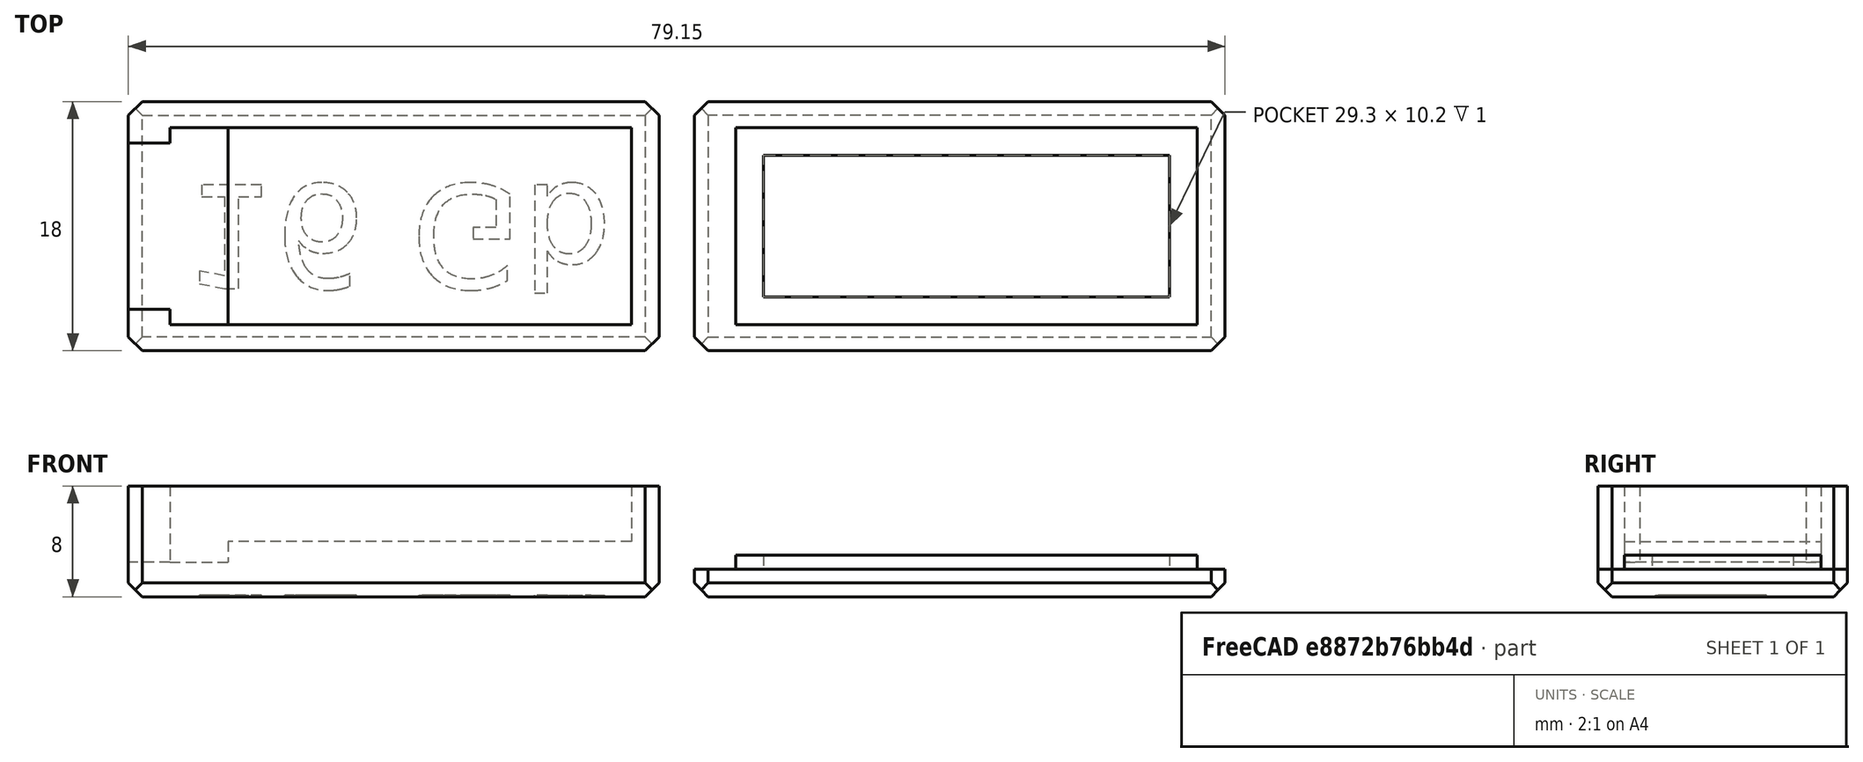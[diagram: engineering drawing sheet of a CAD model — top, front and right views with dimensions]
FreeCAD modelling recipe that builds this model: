
FCSTD DOCUMENT  (FreeCAD 0.21R33668 +26 (Git))
Label: flash_Case
License: All rights reserved
LicenseURL: http://en.wikipedia.org/wiki/All_rights_reserved
objects: TechDraw::DrawViewDimension×17, Sketcher::SketchObject×6, PartDesign::Pocket×4, PartDesign::Chamfer×4, PartDesign::Pad×3, PartDesign::Body×2, TechDraw::DrawViewPart×2, Part::Part2DObjectPython×1, TechDraw::DrawSVGTemplate×1, TechDraw::DrawPage×1
note: 59 computed .brp shape members not serialized (recipe doc carries the construction recipe); baked Part::Feature solids carry a one-line shape summary decoded from their .brp

FEATURE [Sketcher::SketchObject] Sketch
  FullyConstrained = true
  MapMode = 5
  Support = -> [XY_Plane]
  sketch-geometry (4):
    g0: LineSegment StartX=0 StartY=9 StartZ=0 EndX=38.3 EndY=9 EndZ=0
    g1: LineSegment StartX=38.3 StartY=9 StartZ=0 EndX=38.3 EndY=-9 EndZ=0
    g2: LineSegment StartX=38.3 StartY=-9 StartZ=0 EndX=0 EndY=-9 EndZ=0
    g3: LineSegment StartX=0 StartY=-9 StartZ=0 EndX=0 EndY=9 EndZ=0
  constraints (11):
    c: Coincident(g0,g1)
    c: Coincident(g1,g2)
    c: Coincident(g2,g3)
    c: Coincident(g3,g0)
    c: Horizontal(g0)
    c: Horizontal(g2)
    c: Vertical(g1)
    c: Vertical(g3)
    c: DistanceX(g0,g0) = 38.3
    c: DistanceY(g1,g1) = 18
    c: Symmetric(g0,g2,g-1)
FEATURE [PartDesign::Pad] Pad
  Direction = (0,0,1)
  Length = 8
  Length2 = 10
  Profile = -> Sketch
  ReferenceAxis = -> Sketch [N_Axis]
  Type = 0
FEATURE [Sketcher::SketchObject] Sketch001
  ExternalGeometry = -> [Pad]
  FullyConstrained = true
  MapMode = 5
  Placement = pos=(0,0,8) rot=(0,0,1;0rad)
  Support = -> [Pad]
  sketch-geometry (9):
    g0: LineSegment StartX=0 StartY=6 StartZ=0 EndX=0 EndY=-6 EndZ=0
    g1: LineSegment StartX=0 StartY=-6 StartZ=0 EndX=3 EndY=-6 EndZ=0
    g2: LineSegment StartX=3 StartY=6 StartZ=0 EndX=0 EndY=6 EndZ=0
    g3: GeomPoint X=1.5 Y=0 Z=0
    g4: LineSegment StartX=3 StartY=6 StartZ=0 EndX=3 EndY=7.1 EndZ=0
    g5: LineSegment StartX=3 StartY=7.1 StartZ=0 EndX=7.2 EndY=7.1 EndZ=0
    g6: LineSegment StartX=7.2 StartY=7.1 StartZ=0 EndX=7.2 EndY=-7.1 EndZ=0
    g7: LineSegment StartX=7.2 StartY=-7.1 StartZ=0 EndX=3 EndY=-7.1 EndZ=0
    g8: LineSegment StartX=3 StartY=-7.1 StartZ=0 EndX=3 EndY=-6 EndZ=0
  constraints (25):
    c: Coincident(g0,g1)
    c: Coincident(g2,g0)
    c: Horizontal(g1)
    c: Horizontal(g2)
    c: Vertical(g0)
    c: Symmetric(g1,g0,g3)
    c: PointOnObject(g3,g-1)
    c: PointOnObject(g0,g-3)
    c: DistanceY(g0,g0) = 12
    c: DistanceX(g2,g2) = 3
    c: Equal(g1,g2)
    c: Vertical(g4)
    c: Coincident(g4,g5)
    c: Horizontal(g5)
    c: Coincident(g5,g6)
    c: Vertical(g6)
    c: Coincident(g6,g7)
    c: Horizontal(g7)
    c: Coincident(g7,g8)
    c: Coincident(g4,g2)
    c: Coincident(g8,g1)
    c: DistanceY(g6,g5) = 14.2
    c: DistanceX(g4,g5) = 4.2
    c: Vertical(g8)
    c: Equal(g8,g4)
FEATURE [PartDesign::Pocket] Pocket
  BaseFeature = -> Pad
  Direction = (0,0,-1)
  Length = 5.5
  Length2 = 5
  Profile = -> Sketch001
  ReferenceAxis = -> Sketch001 [N_Axis]
  Type = 0
FEATURE [Sketcher::SketchObject] Sketch002
  ExternalGeometry = -> [Pocket]
  FullyConstrained = true
  MapMode = 5
  Placement = pos=(0,0,8) rot=(0,0,1;0rad)
  Support = -> [Pocket]
  sketch-geometry (5):
    g0: LineSegment StartX=36.3 StartY=-7.1 StartZ=0 EndX=36.3 EndY=7.1 EndZ=0
    g1: LineSegment StartX=36.3 StartY=7.1 StartZ=0 EndX=7.2 EndY=7.1 EndZ=0
    g2: LineSegment StartX=7.2 StartY=7.1 StartZ=0 EndX=7.2 EndY=-7.1 EndZ=0
    g3: LineSegment StartX=7.2 StartY=-7.1 StartZ=0 EndX=36.3 EndY=-7.1 EndZ=0
    g4: GeomPoint X=21.75 Y=0 Z=0
  constraints (12):
    c: Coincident(g0,g1)
    c: Coincident(g1,g2)
    c: Coincident(g2,g3)
    c: Coincident(g3,g0)
    c: Horizontal(g1)
    c: Horizontal(g3)
    c: Vertical(g0)
    c: Vertical(g2)
    c: Symmetric(g1,g0,g4)
    c: PointOnObject(g4,g-1)
    c: Coincident(g1,g-3)
    c: DistanceX(g1,g1) = 29.1
FEATURE [PartDesign::Pocket] Pocket001
  BaseFeature = -> Pocket
  Direction = (0,0,-1)
  Length = 4
  Length2 = 5
  Profile = -> Sketch002
  ReferenceAxis = -> Sketch002 [N_Axis]
  Type = 0
FEATURE [PartDesign::Chamfer] Chamfer
  Angle = 45
  Base = -> Pocket001 [Edge3,Edge5,Edge15,Edge13]
  BaseFeature = -> Pocket001
  ChamferType = 0
  FlipDirection = false
  Size = 1
  Size2 = 1
  SupportTransform = false
  UseAllEdges = false
FEATURE [PartDesign::Chamfer] Chamfer001
  Angle = 45
  Base = -> Chamfer [Edge7,Edge27,Edge4,Edge1]
  BaseFeature = -> Chamfer
  ChamferType = 0
  FlipDirection = false
  Size = 1
  Size2 = 1
  SupportTransform = false
  UseAllEdges = false
FEATURE [Sketcher::SketchObject] Sketch003
  FullyConstrained = true
  MapMode = 5
  Support = -> [XY_Plane001]
  sketch-geometry (5):
    g0: LineSegment StartX=79.15 StartY=-9 StartZ=0 EndX=79.15 EndY=9 EndZ=0
    g1: LineSegment StartX=79.15 StartY=9 StartZ=0 EndX=40.85 EndY=9 EndZ=0
    g2: LineSegment StartX=40.85 StartY=9 StartZ=0 EndX=40.85 EndY=-9 EndZ=0
    g3: LineSegment StartX=40.85 StartY=-9 StartZ=0 EndX=79.15 EndY=-9 EndZ=0
    g4: GeomPoint X=60 Y=0 Z=0
  constraints (13):
    c: Coincident(g0,g1)
    c: Coincident(g1,g2)
    c: Coincident(g2,g3)
    c: Coincident(g3,g0)
    c: Horizontal(g1)
    c: Horizontal(g3)
    c: Vertical(g0)
    c: Vertical(g2)
    c: Symmetric(g1,g0,g4)
    c: PointOnObject(g4,g-1)
    c: DistanceX(g1,g1) = 38.3
    c: DistanceY(g2,g2) = 18
    c: DistanceX(g-1,g4) = 60
FEATURE [PartDesign::Pad] Pad001
  Direction = (0,0,1)
  Length = 2
  Length2 = 10
  Profile = -> Sketch003
  ReferenceAxis = -> Sketch003 [N_Axis]
  Type = 0
FEATURE [PartDesign::Chamfer] Chamfer002
  Angle = 45
  Base = -> Pad001 [Edge6,Edge9,Edge11,Edge3]
  BaseFeature = -> Pad001
  ChamferType = 0
  FlipDirection = false
  Size = 1
  Size2 = 1
  SupportTransform = false
  UseAllEdges = false
FEATURE [PartDesign::Chamfer] Chamfer003
  Angle = 45
  Base = -> Chamfer002 [Edge4,Edge14,Edge1,Edge5]
  BaseFeature = -> Chamfer002
  ChamferType = 0
  FlipDirection = false
  Size = 1
  Size2 = 1
  SupportTransform = false
  UseAllEdges = false
FEATURE [Sketcher::SketchObject] Sketch004
  ExternalGeometry = -> [Chamfer003]
  FullyConstrained = true
  MapMode = 5
  Placement = pos=(0,0,2) rot=(0,0,1;0rad)
  Support = -> [Chamfer003]
  sketch-geometry (5):
    g0: LineSegment StartX=43.85 StartY=7.1 StartZ=0 EndX=43.85 EndY=-7.1 EndZ=0
    g1: LineSegment StartX=43.85 StartY=-7.1 StartZ=0 EndX=77.15 EndY=-7.1 EndZ=0
    g2: LineSegment StartX=77.15 StartY=-7.1 StartZ=0 EndX=77.15 EndY=7.1 EndZ=0
    g3: LineSegment StartX=77.15 StartY=7.1 StartZ=0 EndX=43.85 EndY=7.1 EndZ=0
    g4: GeomPoint X=60.5 Y=3e-16 Z=0
  constraints (13):
    c: Coincident(g0,g1)
    c: Coincident(g1,g2)
    c: Coincident(g2,g3)
    c: Coincident(g3,g0)
    c: Horizontal(g1)
    c: Horizontal(g3)
    c: Vertical(g0)
    c: Vertical(g2)
    c: Symmetric(g1,g0,g4)
    c: PointOnObject(g4,g-1)
    c: DistanceX(g-3,g0) = 3
    c: DistanceX(g3,g3) = 33.3
    c: DistanceY(g1,g2) = 14.2
FEATURE [PartDesign::Pad] Pad002
  BaseFeature = -> Chamfer003
  Direction = (0,0,1)
  Length = 1
  Length2 = 10
  Profile = -> Sketch004
  ReferenceAxis = -> Sketch004 [N_Axis]
  Type = 0
FEATURE [Sketcher::SketchObject] Sketch005
  ExternalGeometry = -> [Pad002]
  FullyConstrained = true
  MapMode = 5
  Placement = pos=(0,0,3) rot=(0,0,1;0rad)
  Support = -> [Pad002]
  sketch-geometry (5):
    g0: LineSegment StartX=75.15 StartY=-5.1 StartZ=0 EndX=75.15 EndY=5.1 EndZ=0
    g1: LineSegment StartX=75.15 StartY=5.1 StartZ=0 EndX=45.85 EndY=5.1 EndZ=0
    g2: LineSegment StartX=45.85 StartY=5.1 StartZ=0 EndX=45.85 EndY=-5.1 EndZ=0
    g3: LineSegment StartX=45.85 StartY=-5.1 StartZ=0 EndX=75.15 EndY=-5.1 EndZ=0
    g4: GeomPoint X=60.5 Y=0 Z=0
  constraints (13):
    c: Coincident(g0,g1)
    c: Coincident(g1,g2)
    c: Coincident(g2,g3)
    c: Coincident(g3,g0)
    c: Horizontal(g1)
    c: Horizontal(g3)
    c: Vertical(g0)
    c: Vertical(g2)
    c: Symmetric(g1,g0,g4)
    c: PointOnObject(g4,g-1)
    c: DistanceX(g-3,g1) = 2
    c: Distance(g0,g-4) = 2
    c: Distance(g0,g-5) = 2
FEATURE [PartDesign::Pocket] Pocket002
  BaseFeature = -> Pad002
  Direction = (0,0,-1)
  Length = 1
  Length2 = 5
  Profile = -> Sketch005
  ReferenceAxis = -> Sketch005 [N_Axis]
  Type = 0
FEATURE [PartDesign::Body] Body001  label="Cover"
  Group = -> [Sketch003,Pad001,Chamfer002,Chamfer003,Sketch004,Pad002,Sketch005,Pocket002]
  Origin = -> Origin001
  Tip = -> Pocket002
FEATURE [Part::Part2DObjectPython] ShapeString  # Draft 2D object (typed FeaturePython)
  FontFile = <path>
  MakeFace = true
  Placement = pos=(4,3,0) rot=(1,0,0;3.14159rad)
  Size = 8
  String = 16 Gb
  Tracking = 0
FEATURE [PartDesign::Pocket] Pocket003
  BaseFeature = -> Chamfer001
  Direction = (0,0,1)
  Length = 0.1
  Length2 = 5
  Profile = -> ShapeString
  ReferenceAxis = -> ShapeString [N_Axis]
  Type = 0
FEATURE [PartDesign::Body] Body  label="Тело"
  Group = -> [Sketch,Pad,Sketch001,Pocket,Sketch002,Pocket001,Chamfer,Chamfer001,ShapeString,Pocket003]
  Origin = -> Origin
  Tip = -> Pocket003
FEATURE [TechDraw::DrawSVGTemplate] Template
  Height = 210
  Orientation = 1
  Template = C:/Program Files/FreeCAD 0.21/data/Mod/TechDraw/Templates/A4_Landscape_blank.svg
  Width = 297
FEATURE [TechDraw::DrawViewPart] View001
  CoarseView = false
  Direction = (0,0,1)
  Focus = 100
  HardHidden = false
  IsoCount = 0
  IsoHidden = false
  IsoVisible = false
  LockPosition = false
  Perspective = false
  Rotation = 0
  Scale = 4
  ScaleType = 2
  ScrubCount = 0
  SeamHidden = false
  SeamVisible = false
  SmoothHidden = false
  SmoothVisible = true
  Source = -> [Pocket003]
  X = 133.304
  XDirection = (1,0,0)
  Y = 154.662
FEATURE [TechDraw::DrawViewDimension] Dimension
  AngleOverride = false
  Arbitrary = false
  ArbitraryTolerances = false
  EqualTolerance = true
  ExtensionAngle = 0
  FormatSpec = %.2w
  FormatSpecOverTolerance = %+.2w
  FormatSpecUnderTolerance = %+.2w
  Inverted = false
  LineAngle = 0
  LockPosition = false
  MeasureType = 1
  OverTolerance = 0
  References2D = -> [View001]
  Rotation = 0
  ScaleType = 0
  TheoreticalExact = false
  Type = 1
  UnderTolerance = 0
  X = 2.26455
  Y = -16.8084
FEATURE [TechDraw::DrawViewDimension] Dimension001
  AngleOverride = false
  Arbitrary = false
  ArbitraryTolerances = false
  EqualTolerance = true
  ExtensionAngle = 0
  FormatSpec = %.2w
  FormatSpecOverTolerance = %+.2w
  FormatSpecUnderTolerance = %+.2w
  Inverted = false
  LineAngle = 0
  LockPosition = false
  MeasureType = 1
  OverTolerance = 0
  References2D = -> [View001]
  Rotation = 0
  ScaleType = 0
  TheoreticalExact = false
  Type = 2
  UnderTolerance = 0
  X = 58.4585
  Y = 2.75519
FEATURE [TechDraw::DrawViewDimension] Dimension002
  AngleOverride = false
  Arbitrary = false
  ArbitraryTolerances = false
  EqualTolerance = true
  ExtensionAngle = 0
  FormatSpec = %.2w
  FormatSpecOverTolerance = %+.2w
  FormatSpecUnderTolerance = %+.2w
  Inverted = false
  LineAngle = 0
  LockPosition = false
  MeasureType = 1
  OverTolerance = 0
  References2D = -> [View001]
  Rotation = 0
  ScaleType = 0
  TheoreticalExact = false
  Type = 2
  UnderTolerance = 0
  X = -86.5106
  Y = 1.29138
FEATURE [TechDraw::DrawViewDimension] Dimension003
  AngleOverride = false
  Arbitrary = false
  ArbitraryTolerances = false
  EqualTolerance = true
  ExtensionAngle = 0
  FormatSpec = %.2w
  FormatSpecOverTolerance = %+.2w
  FormatSpecUnderTolerance = %+.2w
  Inverted = false
  LineAngle = 0
  LockPosition = false
  MeasureType = 1
  OverTolerance = 0
  References2D = -> [View001]
  Rotation = 0
  ScaleType = 0
  TheoreticalExact = false
  Type = 2
  UnderTolerance = 0
  X = 108.447
  Y = 6.35612
FEATURE [TechDraw::DrawViewDimension] Dimension004
  AngleOverride = false
  Arbitrary = false
  ArbitraryTolerances = false
  EqualTolerance = true
  ExtensionAngle = 0
  FormatSpec = %.2w
  FormatSpecOverTolerance = %+.2w
  FormatSpecUnderTolerance = %+.2w
  Inverted = false
  LineAngle = 0
  LockPosition = false
  MeasureType = 1
  OverTolerance = 0
  References2D = -> [View001]
  Rotation = 0
  ScaleType = 0
  TheoreticalExact = false
  Type = 1
  UnderTolerance = 0
  X = -71.1553
  Y = 24.4729
FEATURE [TechDraw::DrawViewDimension] Dimension005
  AngleOverride = false
  Arbitrary = false
  ArbitraryTolerances = false
  EqualTolerance = true
  ExtensionAngle = 0
  FormatSpec = %.2w
  FormatSpecOverTolerance = %+.2w
  FormatSpecUnderTolerance = %+.2w
  Inverted = false
  LineAngle = 0
  LockPosition = false
  MeasureType = 1
  OverTolerance = 0
  References2D = -> [View001]
  Rotation = 0
  ScaleType = 0
  TheoreticalExact = false
  Type = 1
  UnderTolerance = 0
  X = -56.2
  Y = 24.2526
FEATURE [TechDraw::DrawViewDimension] Dimension006
  AngleOverride = false
  Arbitrary = false
  ArbitraryTolerances = false
  EqualTolerance = true
  ExtensionAngle = 0
  FormatSpec = %.2w
  FormatSpecOverTolerance = %+.2w
  FormatSpecUnderTolerance = %+.2w
  Inverted = false
  LineAngle = 0
  LockPosition = false
  MeasureType = 1
  OverTolerance = 0
  References2D = -> [View001]
  Rotation = 0
  ScaleType = 0
  TheoreticalExact = false
  Type = 1
  UnderTolerance = 0
  X = 73.9929
  Y = -34.4885
FEATURE [TechDraw::DrawViewDimension] Dimension007
  AngleOverride = false
  Arbitrary = false
  ArbitraryTolerances = false
  EqualTolerance = true
  ExtensionAngle = 0
  FormatSpec = %.2w
  FormatSpecOverTolerance = %+.2w
  FormatSpecUnderTolerance = %+.2w
  Inverted = false
  LineAngle = 0
  LockPosition = false
  MeasureType = 1
  OverTolerance = 0
  References2D = -> [View001]
  Rotation = 0
  ScaleType = 0
  TheoreticalExact = false
  Type = 1
  UnderTolerance = 0
  X = -1.1914
  Y = 50.0302
FEATURE [TechDraw::DrawViewPart] View
  CoarseView = false
  Direction = (0,0,1)
  Focus = 100
  HardHidden = false
  IsoCount = 0
  IsoHidden = false
  IsoVisible = false
  LockPosition = false
  Perspective = false
  Rotation = 0
  Scale = 2
  ScaleType = 2
  ScrubCount = 0
  SeamHidden = false
  SeamVisible = false
  SmoothHidden = false
  SmoothVisible = true
  Source = -> [Body001]
  X = 120.621
  XDirection = (1,0,0)
  Y = 61.8661
FEATURE [TechDraw::DrawViewDimension] Dimension008
  AngleOverride = false
  Arbitrary = false
  ArbitraryTolerances = false
  EqualTolerance = true
  ExtensionAngle = 0
  FormatSpec = %.2w
  FormatSpecOverTolerance = %+.2w
  FormatSpecUnderTolerance = %+.2w
  Inverted = false
  LineAngle = 0
  LockPosition = false
  MeasureType = 1
  OverTolerance = 0
  References2D = -> [View]
  Rotation = 0
  ScaleType = 0
  TheoreticalExact = false
  Type = 2
  UnderTolerance = 0
  X = 68.3874
  Y = 3.55205
FEATURE [TechDraw::DrawViewDimension] Dimension009
  AngleOverride = false
  Arbitrary = false
  ArbitraryTolerances = false
  EqualTolerance = true
  ExtensionAngle = 0
  FormatSpec = %.2w
  FormatSpecOverTolerance = %+.2w
  FormatSpecUnderTolerance = %+.2w
  Inverted = false
  LineAngle = 0
  LockPosition = false
  MeasureType = 1
  OverTolerance = 0
  References2D = -> [View]
  Rotation = 0
  ScaleType = 0
  TheoreticalExact = false
  Type = 2
  UnderTolerance = 0
  X = 49.0286
  Y = 18.6
FEATURE [TechDraw::DrawViewDimension] Dimension010
  AngleOverride = false
  Arbitrary = false
  ArbitraryTolerances = false
  EqualTolerance = true
  ExtensionAngle = 0
  FormatSpec = %.2w
  FormatSpecOverTolerance = %+.2w
  FormatSpecUnderTolerance = %+.2w
  Inverted = false
  LineAngle = 0
  LockPosition = false
  MeasureType = 1
  OverTolerance = 0
  References2D = -> [View]
  Rotation = 0
  ScaleType = 0
  TheoreticalExact = false
  Type = 2
  UnderTolerance = 0
  X = 59.9833
  Y = 14.1619
FEATURE [TechDraw::DrawViewDimension] Dimension011
  AngleOverride = false
  Arbitrary = false
  ArbitraryTolerances = false
  EqualTolerance = true
  ExtensionAngle = 0
  FormatSpec = %.2w
  FormatSpecOverTolerance = %+.2w
  FormatSpecUnderTolerance = %+.2w
  Inverted = false
  LineAngle = 0
  LockPosition = false
  MeasureType = 1
  OverTolerance = 0
  References2D = -> [View]
  Rotation = 0
  ScaleType = 0
  TheoreticalExact = false
  Type = 1
  UnderTolerance = 0
  X = 6.78625
  Y = -34.319
FEATURE [TechDraw::DrawViewDimension] Dimension012
  AngleOverride = false
  Arbitrary = false
  ArbitraryTolerances = false
  EqualTolerance = true
  ExtensionAngle = 0
  FormatSpec = %.2w
  FormatSpecOverTolerance = %+.2w
  FormatSpecUnderTolerance = %+.2w
  Inverted = false
  LineAngle = 0
  LockPosition = false
  MeasureType = 1
  OverTolerance = 0
  References2D = -> [View]
  Rotation = 0
  ScaleType = 0
  TheoreticalExact = false
  Type = 1
  UnderTolerance = 0
  X = -35.826
  Y = 31.9547
FEATURE [TechDraw::DrawViewDimension] Dimension013
  AngleOverride = false
  Arbitrary = false
  ArbitraryTolerances = false
  EqualTolerance = true
  ExtensionAngle = 0
  FormatSpec = %.2w
  FormatSpecOverTolerance = %+.2w
  FormatSpecUnderTolerance = %+.2w
  Inverted = false
  LineAngle = 0
  LockPosition = false
  MeasureType = 1
  OverTolerance = 0
  References2D = -> [View]
  Rotation = 0
  ScaleType = 0
  TheoreticalExact = false
  Type = 1
  UnderTolerance = 0
  X = -30.3
  Y = 30.0346
FEATURE [TechDraw::DrawViewDimension] Dimension014
  AngleOverride = false
  Arbitrary = false
  ArbitraryTolerances = false
  EqualTolerance = true
  ExtensionAngle = 0
  FormatSpec = %.2w
  FormatSpecOverTolerance = %+.2w
  FormatSpecUnderTolerance = %+.2w
  Inverted = false
  LineAngle = 0
  LockPosition = false
  MeasureType = 1
  OverTolerance = 0
  References2D = -> [View]
  Rotation = 0
  ScaleType = 0
  TheoreticalExact = false
  Type = 2
  UnderTolerance = 0
  X = -61.9621
  Y = 3.02602
FEATURE [TechDraw::DrawViewDimension] Dimension015
  AngleOverride = false
  Arbitrary = false
  ArbitraryTolerances = false
  EqualTolerance = true
  ExtensionAngle = 0
  FormatSpec = %.2w
  FormatSpecOverTolerance = %+.2w
  FormatSpecUnderTolerance = %+.2w
  Inverted = false
  LineAngle = 0
  LockPosition = false
  MeasureType = 1
  OverTolerance = 0
  References2D = -> [View001]
  Rotation = 0
  ScaleType = 0
  TheoreticalExact = false
  Type = 2
  UnderTolerance = 0
  X = 89.9088
  Y = 32.4169
FEATURE [TechDraw::DrawViewDimension] Dimension016
  AngleOverride = false
  Arbitrary = false
  ArbitraryTolerances = false
  EqualTolerance = true
  ExtensionAngle = 0
  FormatSpec = %.2w
  FormatSpecOverTolerance = %+.2w
  FormatSpecUnderTolerance = %+.2w
  Inverted = false
  LineAngle = 0
  LockPosition = false
  MeasureType = 1
  OverTolerance = 0
  References2D = -> [View001]
  Rotation = 0
  ScaleType = 0
  TheoreticalExact = false
  Type = 1
  UnderTolerance = 0
  X = 72.6
  Y = -25.9
FEATURE [TechDraw::DrawPage] Page
  KeepUpdated = true
  NextBalloonIndex = 1
  ProjectionType = 0
  Template = -> Template
  Views = -> [View001,Dimension,Dimension001,Dimension002,Dimension003,Dimension004,Dimension005,Dimension006,Dimension007,View,Dimension008,Dimension009,Dimension010,Dimension011,Dimension012,Dimension013,Dimension014,Dimension015,Dimension016]
note: 1 file-system path scrubbed to <path> (originals preserved in the JSON sidecar)
